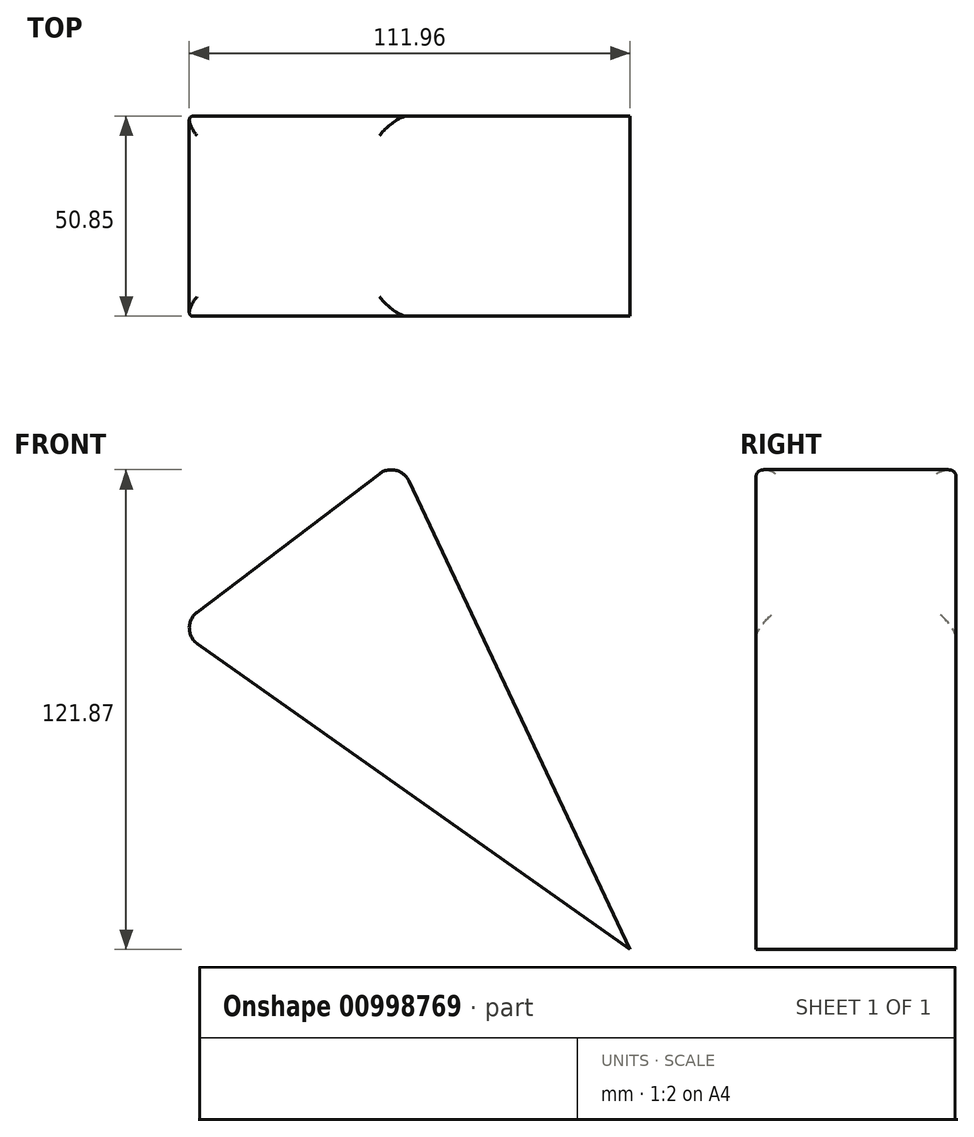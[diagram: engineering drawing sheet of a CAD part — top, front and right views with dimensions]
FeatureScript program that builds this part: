
annotation { "Feature Type Name" : "Feature", "Feature Type Description" : "" }
export const myFeature = defineFeature(function(context is Context, id is Id, definition is map)
    precondition{}
    {
        {
            var Q0;
            Q0=qCreatedBy(makeId("Front.planeOp"),FACE);
            var sketch = newSketch(context, id + "F0", { "sketchPlane" : qUnion([Q0])});
            skLineSegment(sketch, "E0", {"start": v(1.51, 43.05) * mm, "end": v(-55.12, 0) * mm});
            skLineSegment(sketch, "E1", {"start": v(-55.12, 0) * mm, "end": v(60.3, -81.53) * mm});
            skLineSegment(sketch, "E2", {"start": v(60.3, -81.53) * mm, "end": v(1.51, 43.05) * mm});
            skSolve(sketch);
        }
        {
            var Q0;
            Q0=makeQuery(id+"F0.imprint","IMPRINT",FACE,{"disambiguationData":[TD([[makeQuery(id+"F0.imprint","IMPRINT",EDGE,{"derivedFrom":sQuery(id+"F0.wireOp",EDGE,"E0")}),1.0]])]});
            extrude(context, id + "F1", {"entities" : qUnion([Q0]), "depth" : 50.85 * mm, "offsetDistance" : 25 * mm});
        }
        {
            var Q0;
            Q0=makeQuery(id+"F1.opExtrude","SWEPT_FACE",FACE,{"disambiguationData":[OSD([sQuery(id+"F0.wireOp",EDGE,"E0")])]});
            fillet(context, id + "F2", {"entities" : qUnion([Q0]), "radius" : 5 * mm, "tangentPropagation" : true, "allowEdgeOverflow" : false});
        }
    });
